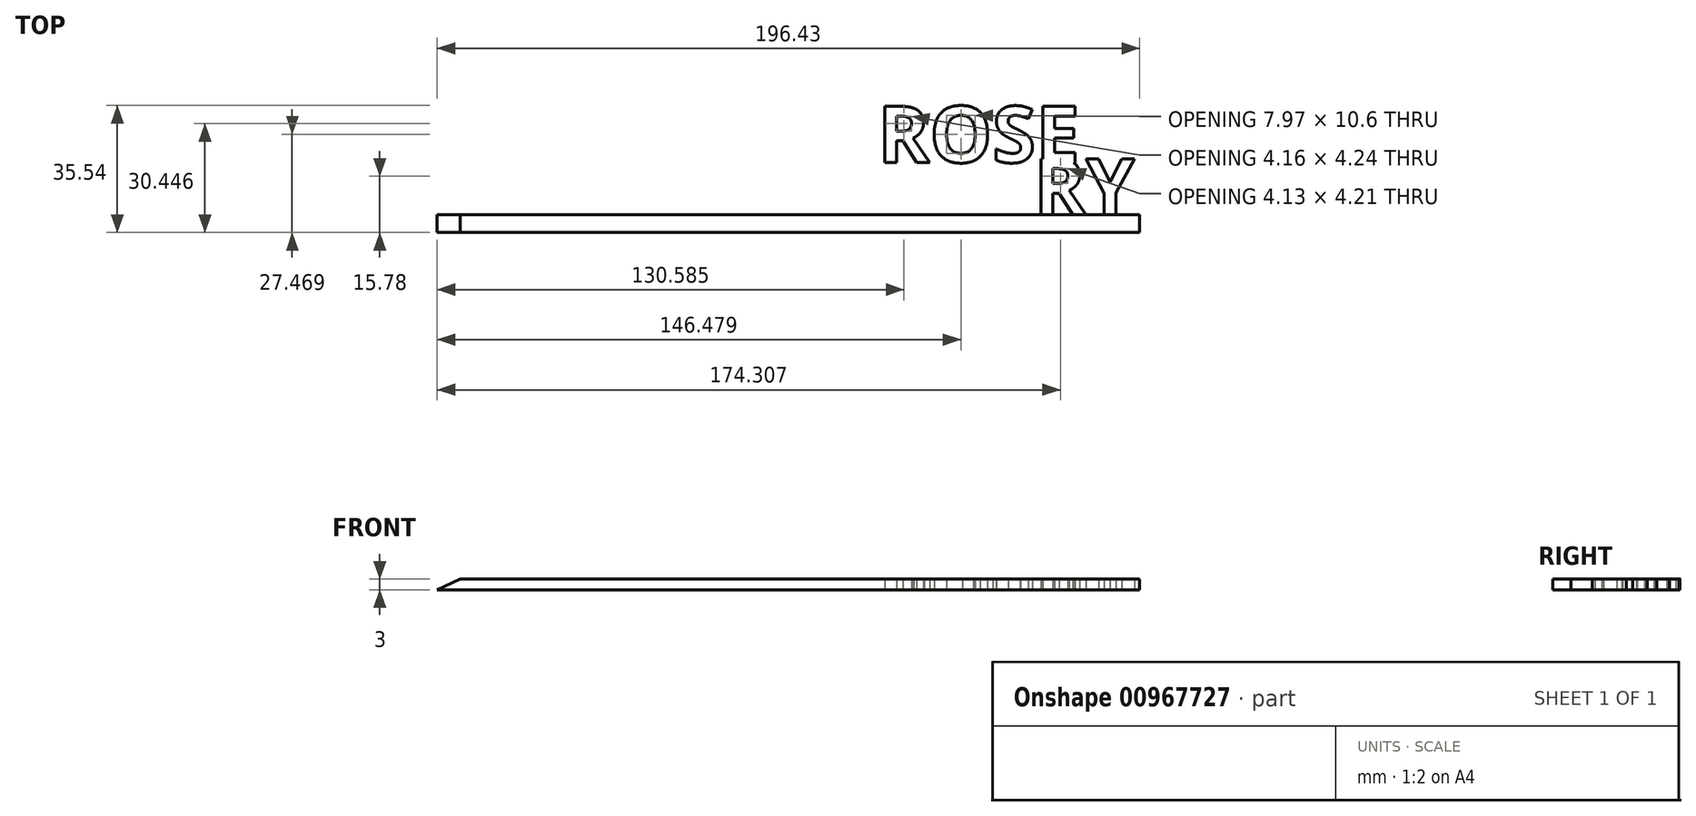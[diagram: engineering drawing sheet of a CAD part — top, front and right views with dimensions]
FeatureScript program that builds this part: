
annotation { "Feature Type Name" : "Feature", "Feature Type Description" : "" }
export const myFeature = defineFeature(function(context is Context, id is Id, definition is map)
    precondition{}
    {
        {
            var Q0;
            Q0=qCreatedBy(makeId("Top.planeOp"),FACE);
            var sketch = newSketch(context, id + "F0", { "sketchPlane" : qUnion([Q0])});
            skLineSegment(sketch, "E0.bottom", {"start": v(65.13, -15.73) * mm, "end": v(-134.87, -15.73) * mm});
            skLineSegment(sketch, "E0.top", {"start": v(65.13, -20.73) * mm, "end": v(-134.87, -20.73) * mm});
            skLineSegment(sketch, "E0.left", {"start": v(65.13, -15.73) * mm, "end": v(65.13, -20.73) * mm});
            skLineSegment(sketch, "E0.right", {"start": v(-134.87, -15.73) * mm, "end": v(-134.87, -20.73) * mm});
            skText(sketch, "E1", { "text": "MARY", "fontName": "NotoSans-Bold.ttf"});
            skText(sketch, "E2", { "text": "ROSE", "fontName": "NotoSans-Bold.ttf"});
            const initialGuessF0  = {"E1": [0, -0.01573, 1, 0, 0.01573], "E2": [-0.0081, -0.00114, 1, 0, 0.01584]};
            skSetInitialGuess(sketch, initialGuessF0);
            skSolve(sketch);
        }
        {
            var Q0;
            Q0=makeQuery(id+"F0.imprint","IMPRINT",FACE,{"disambiguationData":[TD([[makeQuery(id+"F0.imprint","IMPRINT",EDGE,{"derivedFrom":sQuery(id+"F0.wireOp",EDGE,"a65403bf-90fa-4fc5-a389-9b310fcc0066.sketch_text.stroke-93")}),-1.0]])]});
            var Q1;
            {var subQ0=sQuery(id+"F0.wireOp",EDGE,"a65403bf-90fa-4fc5-a389-9b310fcc0066.sketch_text.stroke-82");Q1=makeQuery(id+"F0.imprint","IMPRINT",FACE,{"disambiguationData":[TD([[makeQuery(id+"F0.imprint","IMPRINT",EDGE,{"derivedFrom":subQ0}),-1.0]])]});}
            var Q2;
            {var subQ0=sQuery(id+"F0.wireOp",EDGE,"a65403bf-90fa-4fc5-a389-9b310fcc0066.sketch_text.stroke-75");Q2=makeQuery(id+"F0.imprint","IMPRINT",FACE,{"disambiguationData":[TD([[makeQuery(id+"F0.imprint","IMPRINT",EDGE,{"derivedFrom":subQ0}),-1.0]])]});}
            var Q3;
            Q3=makeQuery(id+"F0.imprint","IMPRINT",FACE,{"disambiguationData":[TD([[makeQuery(id+"F0.imprint","IMPRINT",EDGE,{"derivedFrom":sQuery(id+"F0.wireOp",EDGE,"E0.top")}),-1.0]])]});
            var Q4;
            {var subQ0=sQuery(id+"F0.wireOp",EDGE,"a65403bf-90fa-4fc5-a389-9b310fcc0066.sketch_text.stroke-49");var subQ1=sQuery(id+"F0.wireOp",EDGE,"a65403bf-90fa-4fc5-a389-9b310fcc0066.sketch_text.stroke-48");var subQ2=makeQuery(id+"F0.imprint","INTERSECT",VERTEX,{"derivedFrom":[subQ1,subQ0]});Q4=makeQuery(id+"F0.imprint","IMPRINT",FACE,{"disambiguationData":[TD([[makeQuery(id+"F0.imprint","IMPRINT",EDGE,{"disambiguationData":[TD([[subQ2,1.0]])],"derivedFrom":subQ1}),-1.0]])]});}
            var Q5;
            {var subQ6=sQuery(id+"F0.wireOp",EDGE,"a65403bf-90fa-4fc5-a389-9b310fcc0066.sketch_text.stroke-47");Q5=makeQuery(id+"F0.imprint","IMPRINT",FACE,{"disambiguationData":[TD([[makeQuery(id+"F0.imprint","IMPRINT",EDGE,{"derivedFrom":subQ6}),-1.0]])]});}
            var Q6;
            Q6=makeQuery(id+"F0.imprint","IMPRINT",FACE,{"disambiguationData":[TD([[makeQuery(id+"F0.imprint","IMPRINT",EDGE,{"derivedFrom":sQuery(id+"F0.wireOp",EDGE,"a65403bf-90fa-4fc5-a389-9b310fcc0066.sketch_text.stroke-28")}),-1.0]])]});
            var Q7;
            {var subQ4=sQuery(id+"F0.wireOp",EDGE,"a65403bf-90fa-4fc5-a389-9b310fcc0066.sketch_text.stroke-16");Q7=makeQuery(id+"F0.imprint","IMPRINT",FACE,{"disambiguationData":[TD([[makeQuery(id+"F0.imprint","IMPRINT",EDGE,{"derivedFrom":subQ4}),-1.0]])]});}
            var Q8;
            Q8=makeQuery(id+"F0.imprint","IMPRINT",FACE,{"disambiguationData":[TD([[makeQuery(id+"F0.imprint","IMPRINT",EDGE,{"derivedFrom":sQuery(id+"F0.wireOp",EDGE,"a65403bf-90fa-4fc5-a389-9b310fcc0066.sketch_text.stroke-0")}),-1.0]])]});
            extrude(context, id + "F1", {"entities" : qUnion([Q0, Q1, Q2, Q3, Q4, Q5, Q6, Q7, Q8]), "depth" : 3 * mm, "offsetDistance" : 25 * mm});
        }
        {
            var Q0;
            Q0=makeQuery(id+"F1.opExtrude","SWEPT_FACE",FACE,{"disambiguationData":[OSD([sQuery(id+"F0.wireOp",EDGE,"E0.top")])]});
            var sketch = newSketch(context, id + "F2", { "sketchPlane" : qUnion([Q0])});
            skSolve(sketch);
        }
        {
            var Q0;
            Q0=makeQuery(id+"F0.imprint","IMPRINT",FACE,{"disambiguationData":[TD([[makeQuery(id+"F0.imprint","IMPRINT",EDGE,{"derivedFrom":sQuery(id+"F0.wireOp",EDGE,"ca91762b-dc0a-41a9-b2b8-5458b8065d16.sketch_text.stroke-0")}),-1.0]])]});
            var Q1;
            Q1=makeQuery(id+"F0.imprint","IMPRINT",FACE,{"disambiguationData":[TD([[makeQuery(id+"F0.imprint","IMPRINT",EDGE,{"derivedFrom":sQuery(id+"F0.wireOp",EDGE,"ca91762b-dc0a-41a9-b2b8-5458b8065d16.sketch_text.stroke-24")}),-1.0]])]});
            var Q2;
            {var subQ5=sQuery(id+"F0.wireOp",EDGE,"ca91762b-dc0a-41a9-b2b8-5458b8065d16.sketch_text.stroke-39");Q2=makeQuery(id+"F0.imprint","IMPRINT",FACE,{"disambiguationData":[TD([[makeQuery(id+"F0.imprint","IMPRINT",EDGE,{"derivedFrom":subQ5}),-1.0]])]});}
            var Q3;
            {var subQ0=sQuery(id+"F0.wireOp",EDGE,"ca91762b-dc0a-41a9-b2b8-5458b8065d16.sketch_text.stroke-40");var subQ1=sQuery(id+"F0.wireOp",EDGE,"E0.bottom");var subQ2=makeQuery(id+"F0.imprint","INTERSECT",VERTEX,{"derivedFrom":[subQ1,subQ0]});Q3=makeQuery(id+"F0.imprint","IMPRINT",FACE,{"disambiguationData":[TD([[makeQuery(id+"F0.imprint","IMPRINT",EDGE,{"disambiguationData":[TD([[subQ2,-1.0]])],"derivedFrom":subQ1}),1.0]])]});}
            var Q4;
            Q4=makeQuery(id+"F0.imprint","IMPRINT",FACE,{"disambiguationData":[TD([[makeQuery(id+"F0.imprint","IMPRINT",EDGE,{"derivedFrom":sQuery(id+"F0.wireOp",EDGE,"ca91762b-dc0a-41a9-b2b8-5458b8065d16.sketch_text.stroke-70")}),-1.0]])]});
            var Q5;
            Q5=makeQuery(id+"F0.imprint","IMPRINT",FACE,{"disambiguationData":[TD([[makeQuery(id+"F0.imprint","IMPRINT",EDGE,{"derivedFrom":sQuery(id+"F0.wireOp",EDGE,"ca91762b-dc0a-41a9-b2b8-5458b8065d16.sketch_text.stroke-74")}),-1.0]])]});
            extrude(context, id + "F3", {"entities" : qUnion([Q0, Q1, Q2, Q3, Q4, Q5]), "operationType" : NewBodyOperationType.ADD, "depth" : 3 * mm, "offsetDistance" : 25 * mm});
        }
        {
            var Q0;
            Q0=makeQuery(id+"F0.imprint","IMPRINT",FACE,{"disambiguationData":[TD([[makeQuery(id+"F0.imprint","IMPRINT",EDGE,{"derivedFrom":sQuery(id+"F0.wireOp",EDGE,"E1.sketch_text.stroke-0")}),-1.0]])]});
            var Q1;
            Q1=makeQuery(id+"F0.imprint","IMPRINT",FACE,{"disambiguationData":[TD([[makeQuery(id+"F0.imprint","IMPRINT",EDGE,{"derivedFrom":sQuery(id+"F0.wireOp",EDGE,"E2.sketch_text.stroke-0")}),-1.0]])]});
            var Q2;
            {var subQ8=sQuery(id+"F0.wireOp",EDGE,"E1.sketch_text.stroke-10");Q2=makeQuery(id+"F0.imprint","IMPRINT",FACE,{"disambiguationData":[TD([[makeQuery(id+"F0.imprint","IMPRINT",EDGE,{"derivedFrom":subQ8}),1.0]])]});}
            var Q3;
            {var subQ1=sQuery(id+"F0.wireOp",EDGE,"E1.sketch_text.stroke-24");Q3=makeQuery(id+"F0.imprint","IMPRINT",FACE,{"disambiguationData":[TD([[makeQuery(id+"F0.imprint","IMPRINT",EDGE,{"derivedFrom":subQ1}),1.0]])]});}
            var Q4;
            Q4=makeQuery(id+"F0.imprint","IMPRINT",FACE,{"disambiguationData":[TD([[makeQuery(id+"F0.imprint","IMPRINT",EDGE,{"derivedFrom":sQuery(id+"F0.wireOp",EDGE,"E1.sketch_text.stroke-19")}),-1.0]])]});
            var Q5;
            Q5=makeQuery(id+"F0.imprint","IMPRINT",FACE,{"disambiguationData":[TD([[makeQuery(id+"F0.imprint","IMPRINT",EDGE,{"derivedFrom":sQuery(id+"F0.wireOp",EDGE,"E1.sketch_text.stroke-31")}),-1.0]])]});
            var Q6;
            {var subQ7=sQuery(id+"F0.wireOp",EDGE,"E2.sketch_text.stroke-63");Q6=makeQuery(id+"F0.imprint","IMPRINT",FACE,{"disambiguationData":[TD([[makeQuery(id+"F0.imprint","IMPRINT",EDGE,{"derivedFrom":subQ7}),-1.0]])]});}
            var Q7;
            Q7=makeQuery(id+"F0.imprint","IMPRINT",FACE,{"disambiguationData":[TD([[makeQuery(id+"F0.imprint","IMPRINT",EDGE,{"derivedFrom":sQuery(id+"F0.wireOp",EDGE,"E1.sketch_text.stroke-50")}),-1.0]])]});
            var Q8;
            {var subQ0=sQuery(id+"F0.wireOp",EDGE,"E1.sketch_text.stroke-42");var subQ1=sQuery(id+"F0.wireOp",EDGE,"E1.sketch_text.stroke-41");var subQ2=makeQuery(id+"F0.imprint","INTERSECT",VERTEX,{"derivedFrom":[subQ1,subQ0]});Q8=makeQuery(id+"F0.imprint","IMPRINT",FACE,{"disambiguationData":[TD([[makeQuery(id+"F0.imprint","IMPRINT",EDGE,{"disambiguationData":[TD([[subQ2,1.0]])],"derivedFrom":subQ1}),-1.0]])]});}
            var Q9;
            {var subQ5=sQuery(id+"F0.wireOp",EDGE,"E1.sketch_text.stroke-24");Q9=makeQuery(id+"F0.imprint","IMPRINT",FACE,{"disambiguationData":[TD([[makeQuery(id+"F0.imprint","IMPRINT",EDGE,{"derivedFrom":subQ5}),-1.0]])]});}
            var Q10;
            {var subQ5=sQuery(id+"F0.wireOp",EDGE,"E1.sketch_text.stroke-10");Q10=makeQuery(id+"F0.imprint","IMPRINT",FACE,{"disambiguationData":[TD([[makeQuery(id+"F0.imprint","IMPRINT",EDGE,{"derivedFrom":subQ5}),-1.0]])]});}
            var Q11;
            {var subQ5=sQuery(id+"F0.wireOp",EDGE,"E2.sketch_text.stroke-16");Q11=makeQuery(id+"F0.imprint","IMPRINT",FACE,{"disambiguationData":[TD([[makeQuery(id+"F0.imprint","IMPRINT",EDGE,{"derivedFrom":subQ5}),-1.0]])]});}
            extrude(context, id + "F4", {"entities" : qUnion([Q0, Q1, Q2, Q3, Q4, Q5, Q6, Q7, Q8, Q9, Q10, Q11]), "operationType" : NewBodyOperationType.ADD, "depth" : 3 * mm, "offsetDistance" : 25 * mm});
        }
        {
            var Q0;
            Q0=makeQuery(id+"F1.opExtrude","CAP_EDGE",EDGE,{"disambiguationData":[OSD([sQuery(id+"F0.wireOp",EDGE,"E0.right")])],"isStart":false});
            chamfer(context, id + "F5", {"entities" : qUnion([Q0]), "chamferType" : ChamferType.OFFSET_ANGLE, "width" : 10 * mm, "oppositeDirection" : false, "angle" : 25 * degree, "tangentPropagation" : true});
        }
    });
